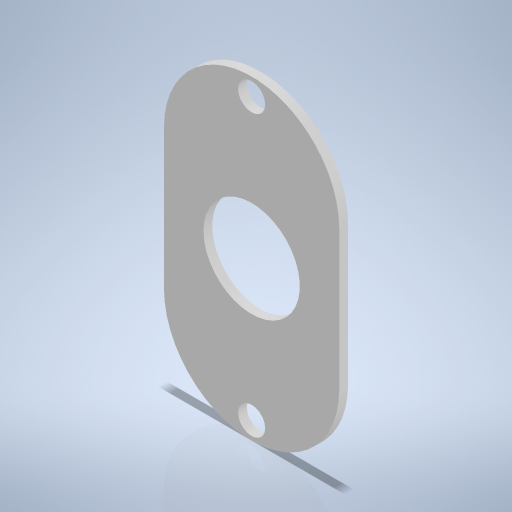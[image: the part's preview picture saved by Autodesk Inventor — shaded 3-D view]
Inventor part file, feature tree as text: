
AUTODESK INVENTOR PART (.ipt)
format: ipt  version: 2024 (Build 280153000, 153)  size: 241,152 bytes
history: native  units: mm
features: sketch x2, hole x2, extrude x1
ambient origin geometry x8: Origin, YZ Plane, XZ Plane, XY Plane, X Axis, Y Axis, Z Axis, Center Point
bodies: Volumenkörper1 (feature_tree)
feature tree (5):
  extrude  "Extrusion1"  Depth=10.0mm
  sketch  "Skizze2"  dims[d2=1.0mm d3=0.0mm d4=3.1mm d5=23.0mm d6=4.0mm d7=2.0mm d8=90.0deg d9=25.0mm d10=20.594885mm d11=32.0mm d12=16.0mm d13=11.0mm d14=6.0mm d15=4.0mm d16=2.0mm d17=90.0deg d18=8.0mm d19=0.0mm]
  hole  "Bohrung1"  [1 undecoded]
  hole  "Bohrung2"  [1 undecoded]
  sketch  "Skizze1"  dims[d0=10.0mm d1=16.0mm]
note: 2 required parameter values undecoded (feature->parameter linkage not recoverable at this tier; creation-order binding heuristic only, values carry confidence <= 0.55)
